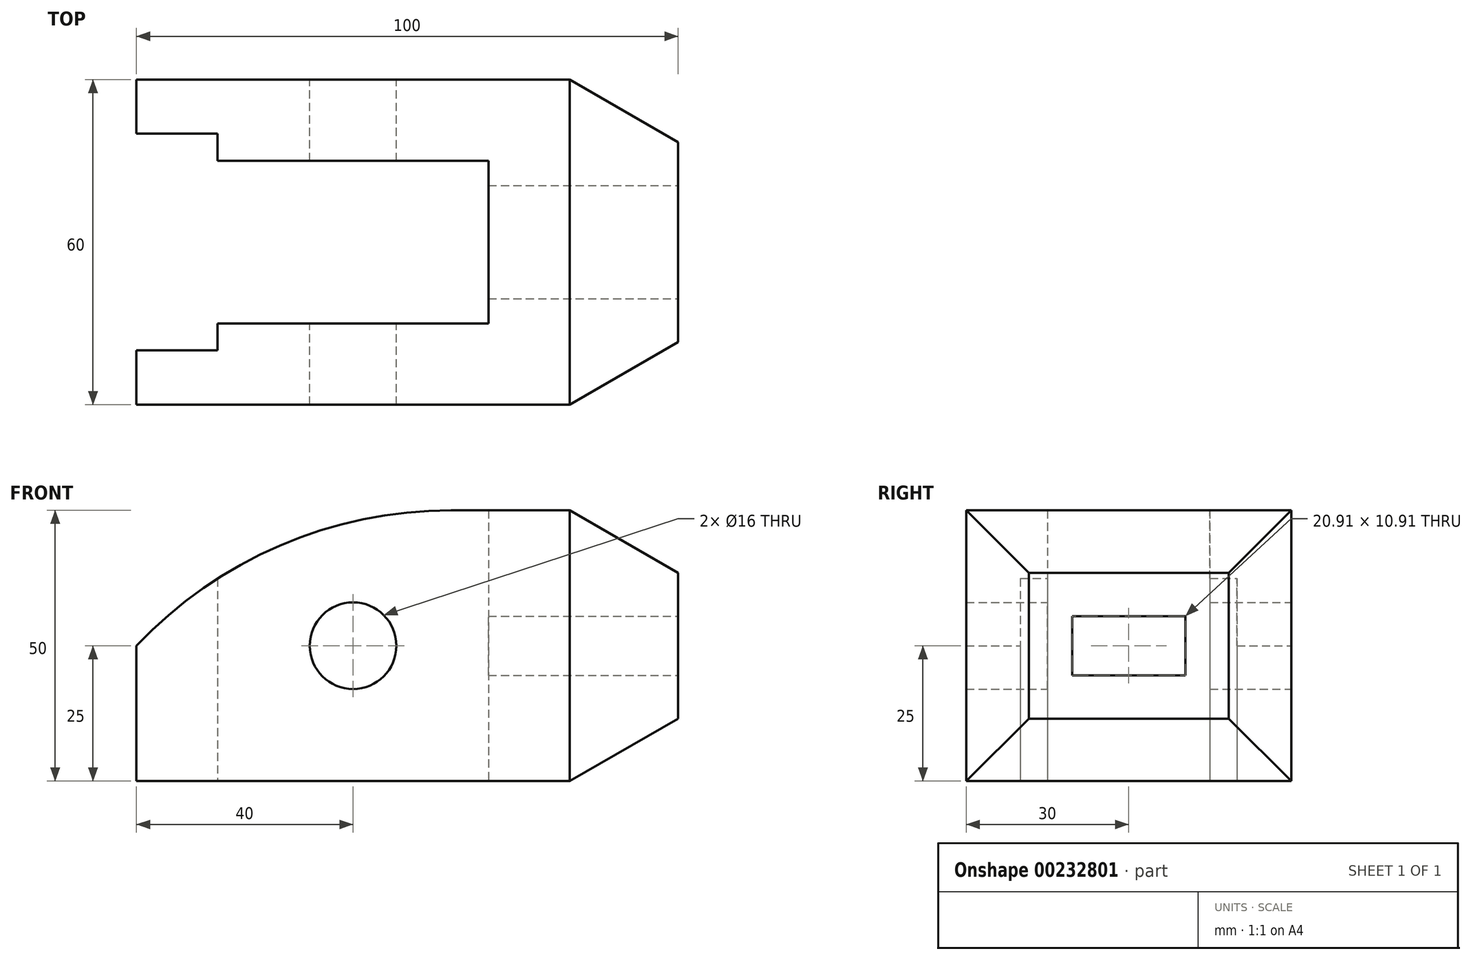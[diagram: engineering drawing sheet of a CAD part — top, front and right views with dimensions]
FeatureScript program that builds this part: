
annotation { "Feature Type Name" : "Feature", "Feature Type Description" : "" }
export const myFeature = defineFeature(function(context is Context, id is Id, definition is map)
    precondition{}
    {
        {
            var Q0;
            Q0=qCreatedBy(makeId("Front.planeOp"),FACE);
            var sketch = newSketch(context, id + "F0", { "sketchPlane" : qUnion([Q0])});
            skLineSegment(sketch, "E0", {"start": v(-80, 0) * mm, "end": v(0, 0) * mm});
            skLineSegment(sketch, "E1", {"start": v(0, 0) * mm, "end": v(0, 50) * mm});
            skLineSegment(sketch, "E2", {"start": v(0, 50) * mm, "end": v(-21.9, 50) * mm});
            skLineSegment(sketch, "E3", {"start": v(-80, 0) * mm, "end": v(-80, 25) * mm});
            skArc(sketch, "E4", {"start": v(-21.9, 50) * mm, "mid": v(-53.53, 43.48) * mm, "end": v(-80, 25) * mm});
            skLineSegment(sketch, "E5", {"start": v(0, 0) * mm, "end": v(20, 11.55) * mm});
            skLineSegment(sketch, "E6", {"start": v(0, 50) * mm, "end": v(20, 38.45) * mm});
            skLineSegment(sketch, "E7", {"start": v(20, 38.45) * mm, "end": v(20, 11.55) * mm});
            skCircle(sketch, "E8", {"center": v(-40, 25) * mm, "radius": 8 * mm});
            skSolve(sketch);
        }
        {
            var Q0;
            Q0 = qSketchRegion(id + "F0", true);
            extrude(context, id + "F1", {"entities" : qUnion([Q0]), "depth" : 60 * mm});
        }
        {
            var Q0;
            Q0=qCreatedBy(makeId("Top.planeOp"),FACE);
            var sketch = newSketch(context, id + "F2", { "sketchPlane" : qUnion([Q0])});
            skLineSegment(sketch, "E9.0.0", {"start": v(-21.9, 0) * mm, "end": v(-80, 0) * mm, "construction": true});
            skLineSegment(sketch, "E9.0.1", {"start": v(-80, 0) * mm, "end": v(-80, -60) * mm, "construction": true});
            skLineSegment(sketch, "E9.0.2", {"start": v(-80, -60) * mm, "end": v(-21.9, -60) * mm, "construction": true});
            skLineSegment(sketch, "E9.0.3", {"start": v(-21.9, -60) * mm, "end": v(-21.9, 0) * mm, "construction": true});
            skLineSegment(sketch, "E10.0.0", {"start": v(0, 0) * mm, "end": v(-21.9, 0) * mm, "construction": true});
            skLineSegment(sketch, "E10.0.1", {"start": v(-21.9, 0) * mm, "end": v(-21.9, -60) * mm, "construction": true});
            skLineSegment(sketch, "E10.0.2", {"start": v(-21.9, -60) * mm, "end": v(0, -60) * mm, "construction": true});
            skLineSegment(sketch, "E10.0.3", {"start": v(0, -60) * mm, "end": v(0, 0) * mm, "construction": true});
            skLineSegment(sketch, "E11.0.0", {"start": v(20, 0) * mm, "end": v(0, 0) * mm, "construction": true});
            skLineSegment(sketch, "E11.0.1", {"start": v(0, 0) * mm, "end": v(0, -60) * mm, "construction": true});
            skLineSegment(sketch, "E11.0.2", {"start": v(0, -60) * mm, "end": v(20, -60) * mm, "construction": true});
            skLineSegment(sketch, "E11.0.3", {"start": v(20, -60) * mm, "end": v(20, 0) * mm, "construction": true});
            skLineSegment(sketch, "E12", {"start": v(0, 0) * mm, "end": v(20, -11.55) * mm});
            skLineSegment(sketch, "E13", {"start": v(0, -60) * mm, "end": v(20, -48.45) * mm});
            skLineSegment(sketch, "E14", {"start": v(20, -11.55) * mm, "end": v(20, 0) * mm});
            skLineSegment(sketch, "E15", {"start": v(20, -48.45) * mm, "end": v(20, -60) * mm});
            skLineSegment(sketch, "E16", {"start": v(-80, -10) * mm, "end": v(-65, -10) * mm});
            skLineSegment(sketch, "E17", {"start": v(-65, -10) * mm, "end": v(-65, -15) * mm});
            skLineSegment(sketch, "E18", {"start": v(-65, -15) * mm, "end": v(-15, -15) * mm});
            skLineSegment(sketch, "E19", {"start": v(-15, -15) * mm, "end": v(-15, -45) * mm});
            skLineSegment(sketch, "E20", {"start": v(-15, -45) * mm, "end": v(-65, -45) * mm});
            skLineSegment(sketch, "E21", {"start": v(-65, -45) * mm, "end": v(-65, -50) * mm});
            skLineSegment(sketch, "E22", {"start": v(-65, -50) * mm, "end": v(-80, -50) * mm});
            skLineSegment(sketch, "E23", {"start": v(-80, -50) * mm, "end": v(-80, -10) * mm});
            skLineSegment(sketch, "E24", {"start": v(0, -60) * mm, "end": v(20, -60) * mm});
            skLineSegment(sketch, "E25", {"start": v(0, 0) * mm, "end": v(20, 0) * mm});
            skSolve(sketch);
        }
        {
            var Q0;
            Q0=makeQuery(id+"F2.imprint","IMPRINT",FACE,{"disambiguationData":[TD([[makeQuery(id+"F2.imprint","IMPRINT",EDGE,{"derivedFrom":sQuery(id+"F2.wireOp",EDGE,"E13")}),-1.0]])]});
            var Q1;
            Q1=makeQuery(id+"F2.imprint","IMPRINT",FACE,{"disambiguationData":[TD([[makeQuery(id+"F2.imprint","IMPRINT",EDGE,{"derivedFrom":sQuery(id+"F2.wireOp",EDGE,"E12")}),1.0]])]});
            var Q2;
            Q2=makeQuery(id+"F2.imprint","IMPRINT",FACE,{"disambiguationData":[TD([[makeQuery(id+"F2.imprint","IMPRINT",EDGE,{"derivedFrom":sQuery(id+"F2.wireOp",EDGE,"E16")}),-1.0]])]});
            extrude(context, id + "F3", {"entities" : qUnion([Q0, Q1, Q2]), "operationType" : NewBodyOperationType.REMOVE, "endBound" : BoundingType.THROUGH_ALL, "depth" : 25 * mm});
        }
        {
            var Q0;
            Q0=qCreatedBy(makeId("Right.planeOp"),FACE);
            cPlane(context, id + "F4", {"entities" : qUnion([Q0]), "cplaneType" : CPlaneType.OFFSET, "offset" : 20 * mm, "width" : 150 * mm, "height" : 150 * mm});
        }
        {
            var Q0;
            Q0=qCreatedBy(id+"F4.planeOp",FACE);
            var sketch = newSketch(context, id + "F5", { "sketchPlane" : qUnion([Q0])});
            skLineSegment(sketch, "E26.bottom", {"start": v(-19.55, 19.55) * mm, "end": v(-40.45, 19.55) * mm});
            skLineSegment(sketch, "E26.top", {"start": v(-19.55, 30.45) * mm, "end": v(-40.45, 30.45) * mm});
            skLineSegment(sketch, "E26.left", {"start": v(-19.55, 19.55) * mm, "end": v(-19.55, 30.45) * mm});
            skLineSegment(sketch, "E26.right", {"start": v(-40.45, 19.55) * mm, "end": v(-40.45, 30.45) * mm});
            skPoint(sketch, "E26.middle", {"position": v(-30, 25) * mm});
            skSolve(sketch);
        }
        {
            var Q0;
            Q0=makeQuery(id+"F5.imprint","IMPRINT",FACE,{"disambiguationData":[TD([[makeQuery(id+"F5.imprint","IMPRINT",EDGE,{"derivedFrom":sQuery(id+"F5.wireOp",EDGE,"E26.bottom")}),-1.0]])]});
            extrude(context, id + "F6", {"entities" : qUnion([Q0]), "operationType" : NewBodyOperationType.REMOVE, "endBound" : BoundingType.THROUGH_ALL, "oppositeDirection" : true, "depth" : 25 * mm});
        }
    });
